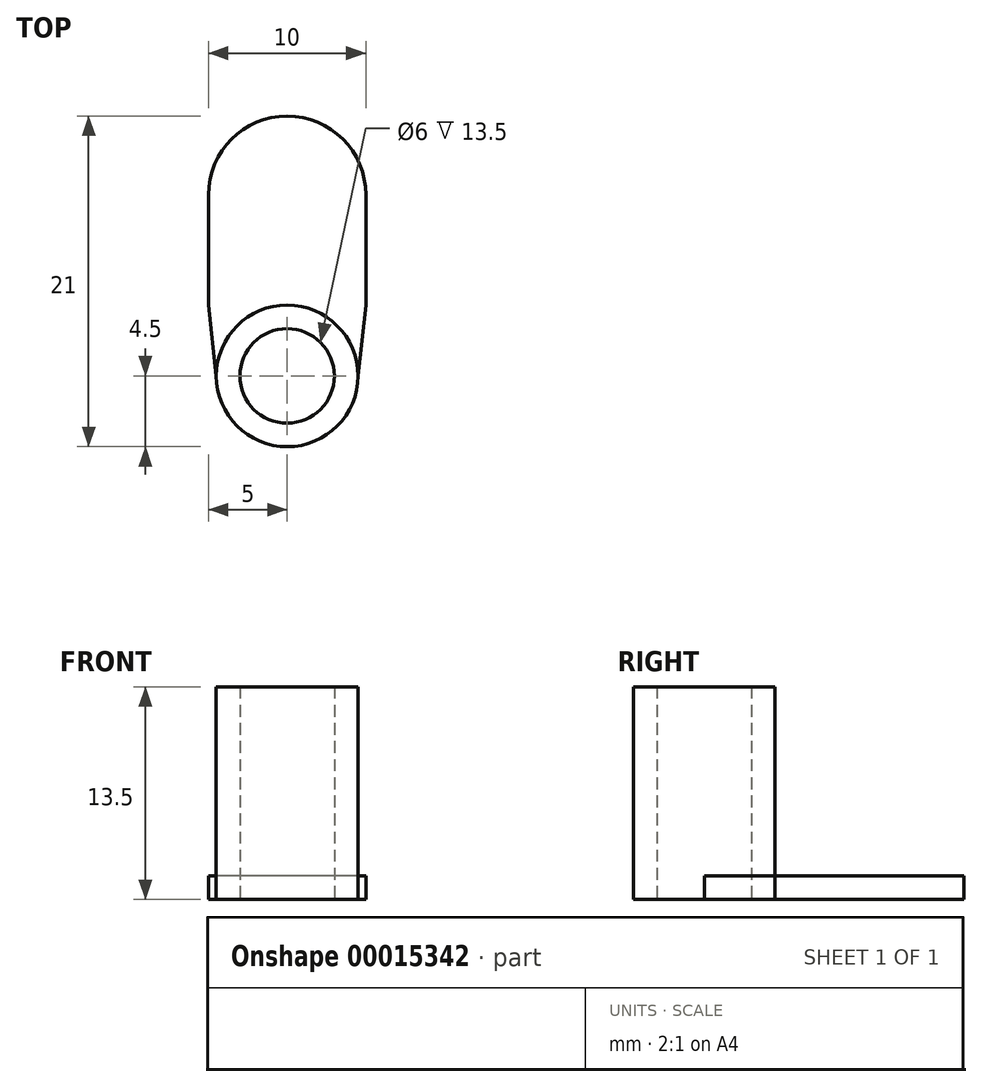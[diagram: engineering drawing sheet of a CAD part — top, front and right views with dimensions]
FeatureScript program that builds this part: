
annotation { "Feature Type Name" : "Feature", "Feature Type Description" : "" }
export const myFeature = defineFeature(function(context is Context, id is Id, definition is map)
    precondition{}
    {
        {
            var Q0;
            Q0=qCreatedBy(makeId("Top.planeOp"),FACE);
            var sketch = newSketch(context, id + "F0", { "sketchPlane" : qUnion([Q0])});
            skLineSegment(sketch, "E0", {"start": v(-5, 0) * mm, "end": v(-5, -0.09) * mm});
            skLineSegment(sketch, "E1", {"start": v(-5, -7) * mm, "end": v(5, -7) * mm});
            skLineSegment(sketch, "E2", {"start": v(5, -7) * mm, "end": v(5, 0) * mm});
            skLineSegment(sketch, "E3", {"start": v(-5, -0.09) * mm, "end": v(-5, -7) * mm});
            skArc(sketch, "E4", {"start": v(5, 0) * mm, "mid": v(0, 5) * mm, "end": v(-5, 0) * mm});
            skLineSegment(sketch, "E5", {"start": v(0, 0) * mm, "end": v(0, -11.5) * mm, "construction": true});
            skCircle(sketch, "E6", {"center": v(0, -11.5) * mm, "radius": 4.5 * mm});
            skLineSegment(sketch, "E7", {"start": v(0, -11.5) * mm, "end": v(4.5, -11.5) * mm, "construction": true});
            skLineSegment(sketch, "E8", {"start": v(5, -7) * mm, "end": v(4.5, -11.5) * mm});
            skLineSegment(sketch, "E9", {"start": v(-4.5, -11.5) * mm, "end": v(-5, -7) * mm});
            skCircle(sketch, "E10", {"center": v(0, -11.5) * mm, "radius": 3 * mm});
            skLineSegment(sketch, "E11", {"start": v(0, -11.5) * mm, "end": v(0, -14.5) * mm, "construction": true});
            skSolve(sketch);
        }
        {
            var Q0;
            Q0=makeQuery(id+"F0.imprint","IMPRINT",FACE,{"disambiguationData":[TD([[makeQuery(id+"F0.imprint","IMPRINT",EDGE,{"derivedFrom":sQuery(id+"F0.wireOp",EDGE,"E10")}),-1.0]])]});
            var Q1;
            Q1=makeQuery(id+"F0.imprint","IMPRINT",FACE,{"disambiguationData":[TD([[makeQuery(id+"F0.imprint","IMPRINT",EDGE,{"derivedFrom":sQuery(id+"F0.wireOp",EDGE,"E0")}),1.0]])]});
            var Q2;
            {var subQ0=sQuery(id+"F0.wireOp",EDGE,"E8");Q2=makeQuery(id+"F0.imprint","IMPRINT",FACE,{"disambiguationData":[TD([[makeQuery(id+"F0.imprint","IMPRINT",EDGE,{"derivedFrom":subQ0}),-1.0]])]});}
            var Q3;
            {var subQ0=sQuery(id+"F0.wireOp",EDGE,"E9");Q3=makeQuery(id+"F0.imprint","IMPRINT",FACE,{"disambiguationData":[TD([[makeQuery(id+"F0.imprint","IMPRINT",EDGE,{"derivedFrom":subQ0}),-1.0]])]});}
            extrude(context, id + "F1", {"entities" : qUnion([Q0, Q1, Q2, Q3]), "depth" : 1.5 * mm});
        }
        {
            var Q0;
            Q0=makeQuery(id+"F1.opExtrude","CAP_FACE",FACE,{"disambiguationData":[OSD([sQuery(id+"F0.wireOp",EDGE,"E0"),sQuery(id+"F0.wireOp",EDGE,"E2"),sQuery(id+"F0.wireOp",EDGE,"E3"),sQuery(id+"F0.wireOp",EDGE,"E4"),sQuery(id+"F0.wireOp",EDGE,"E6"),sQuery(id+"F0.wireOp",EDGE,"E8"),sQuery(id+"F0.wireOp",EDGE,"E9"),sQuery(id+"F0.wireOp",EDGE,"E10")])],"isStart":false});
            var sketch = newSketch(context, id + "F2", { "sketchPlane" : qUnion([Q0])});
            skLineSegment(sketch, "E12", {"start": v(0, -14.5) * mm, "end": v(0, -16) * mm, "construction": true});
            skLineSegment(sketch, "E13", {"start": v(0, -14.5) * mm, "end": v(0, -8.5) * mm, "construction": true});
            skLineSegment(sketch, "E14", {"start": v(3, -11.5) * mm, "end": v(-3, -11.5) * mm, "construction": true});
            skCircle(sketch, "E15", {"center": v(0, -11.5) * mm, "radius": 3 * mm});
            skCircle(sketch, "E16", {"center": v(0, -11.5) * mm, "radius": 4.5 * mm});
            skSolve(sketch);
        }
        {
            var Q0;
            Q0=qSketchRegion(id+"F2",true);
            extrude(context, id + "F3", {"entities" : qUnion([Q0]), "operationType" : NewBodyOperationType.ADD, "depth" : 12 * mm});
        }
    });
